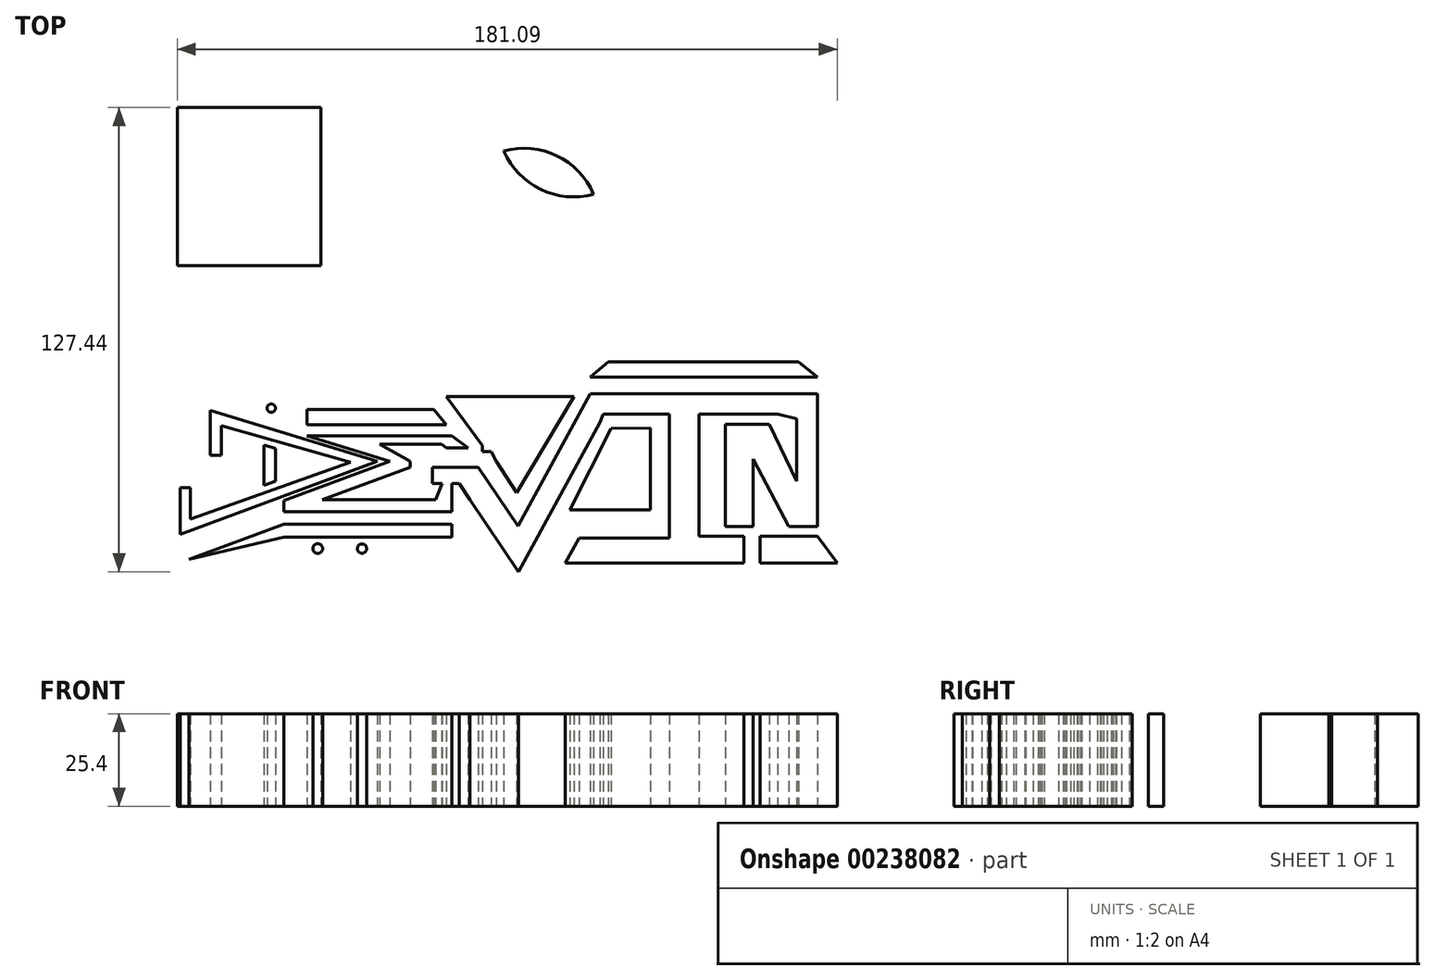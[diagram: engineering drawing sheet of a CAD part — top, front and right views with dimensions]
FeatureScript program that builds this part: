
annotation { "Feature Type Name" : "Feature", "Feature Type Description" : "" }
export const myFeature = defineFeature(function(context is Context, id is Id, definition is map)
    precondition{}
    {
        {
            var Q0;
            Q0=qCreatedBy(makeId("Top.planeOp"),FACE);
            var sketch = newSketch(context, id + "F0", { "sketchPlane" : qUnion([Q0])});
            skLineSegment(sketch, "E0.bottom", {"start": v(-55, 61.65) * mm, "end": v(-22, 61.65) * mm});
            skLineSegment(sketch, "E0.top", {"start": v(-61.34, 18.26) * mm, "end": v(-22, 18.26) * mm});
            skLineSegment(sketch, "E0.left", {"start": v(-61.34, 55.3) * mm, "end": v(-61.34, 18.26) * mm});
            skLineSegment(sketch, "E0.right", {"start": v(-22, 61.65) * mm, "end": v(-22, 18.26) * mm});
            skLineSegment(sketch, "E1.bottom", {"start": v(-41.67, 61.65) * mm, "end": v(-28.35, 61.65) * mm});
            skLineSegment(sketch, "E1.top", {"start": v(-41.67, 39.95) * mm, "end": v(-22, 39.95) * mm});
            skLineSegment(sketch, "E1.left", {"start": v(-41.67, 61.65) * mm, "end": v(-41.67, 39.95) * mm});
            skLineSegment(sketch, "E1.right", {"start": v(-22, 55.3) * mm, "end": v(-22, 39.95) * mm});
            skLineSegment(sketch, "E2.bottom", {"start": v(-41.67, 18.26) * mm, "end": v(-28.35, 18.26) * mm});
            skLineSegment(sketch, "E2.left", {"start": v(-41.67, 18.26) * mm, "end": v(-41.67, 39.95) * mm});
            skLineSegment(sketch, "E2.right", {"start": v(-22, 24.61) * mm, "end": v(-22, 39.95) * mm});
            skLineSegment(sketch, "E3.bottom", {"start": v(-41.67, 39.95) * mm, "end": v(-61.34, 39.95) * mm});
            skLineSegment(sketch, "E3.top", {"start": v(-41.67, 61.65) * mm, "end": v(-61.34, 61.65) * mm});
            skLineSegment(sketch, "E3.left", {"start": v(-41.67, 39.95) * mm, "end": v(-41.67, 61.65) * mm});
            skLineSegment(sketch, "E3.right", {"start": v(-61.34, 39.95) * mm, "end": v(-61.34, 61.65) * mm});
            skLineSegment(sketch, "E4.bottom", {"start": v(-55, 18.26) * mm, "end": v(-41.67, 18.26) * mm});
            skLineSegment(sketch, "E4.top", {"start": v(-61.34, 39.95) * mm, "end": v(-41.67, 39.95) * mm});
            skLineSegment(sketch, "E4.left", {"start": v(-61.34, 24.61) * mm, "end": v(-61.34, 39.95) * mm});
            skPoint(sketch, "E5.visualSharp", {"position": v(-61.34, 61.65) * mm});
            skArc(sketch, "E5.filletArc", {"start": v(-55, 61.65) * mm, "mid": v(-59.48, 59.79) * mm, "end": v(-61.34, 55.3) * mm});
            skPoint(sketch, "E6.visualSharp", {"position": v(-22, 61.65) * mm});
            skArc(sketch, "E6.filletArc", {"start": v(-22, 55.3) * mm, "mid": v(-23.86, 59.79) * mm, "end": v(-28.35, 61.65) * mm});
            skPoint(sketch, "E7.visualSharp", {"position": v(-22, 18.26) * mm});
            skArc(sketch, "E7.filletArc", {"start": v(-28.35, 18.26) * mm, "mid": v(-23.86, 20.12) * mm, "end": v(-22, 24.61) * mm});
            skPoint(sketch, "E8.visualSharp", {"position": v(-61.34, 18.26) * mm});
            skArc(sketch, "E8.filletArc", {"start": v(-61.34, 24.61) * mm, "mid": v(-59.48, 20.12) * mm, "end": v(-55, 18.26) * mm});
            skArc(sketch, "E9", {"start": v(13.52, 35.01) * mm, "mid": v(48.5, 14.76) * mm, "end": v(28.25, 49.74) * mm});
            skArc(sketch, "E10", {"start": v(28.25, 49.74) * mm, "mid": v(67.3, 51.66) * mm, "end": v(36.52, 75.77) * mm});
            skLineSegment(sketch, "E11", {"start": v(-52.26, -21.5) * mm, "end": v(-6.46, -35.41) * mm});
            skLineSegment(sketch, "E12", {"start": v(-6.46, -35.41) * mm, "end": v(-60.54, -55.6) * mm});
            skLineSegment(sketch, "E13", {"start": v(-60.54, -55.6) * mm, "end": v(-60.54, -42.68) * mm});
            skLineSegment(sketch, "E14", {"start": v(-52.26, -21.5) * mm, "end": v(-52.26, -33.8) * mm});
            skLineSegment(sketch, "E15", {"start": v(-52.26, -33.8) * mm, "end": v(-49.26, -33.8) * mm});
            skLineSegment(sketch, "E16", {"start": v(-49.26, -33.8) * mm, "end": v(-49.26, -25.67) * mm});
            skLineSegment(sketch, "E17", {"start": v(-49.26, -25.67) * mm, "end": v(-13.79, -35.76) * mm});
            skLineSegment(sketch, "E18", {"start": v(-13.79, -35.76) * mm, "end": v(-57.75, -51.38) * mm});
            skLineSegment(sketch, "E19", {"start": v(-57.75, -51.38) * mm, "end": v(-57.75, -42.68) * mm});
            skLineSegment(sketch, "E20", {"start": v(-57.75, -42.68) * mm, "end": v(-60.54, -42.68) * mm});
            skLineSegment(sketch, "E21", {"start": v(-37.52, -31.02) * mm, "end": v(-34.41, -31.9) * mm});
            skLineSegment(sketch, "E22", {"start": v(-34.41, -31.9) * mm, "end": v(-34.41, -40.97) * mm});
            skLineSegment(sketch, "E23", {"start": v(-34.41, -40.97) * mm, "end": v(-37.52, -42.07) * mm});
            skLineSegment(sketch, "E24", {"start": v(-37.52, -42.07) * mm, "end": v(-37.52, -31.02) * mm});
            skLineSegment(sketch, "E25", {"start": v(-3, -35.41) * mm, "end": v(-25.8, -28.49) * mm});
            skLineSegment(sketch, "E26", {"start": v(-25.8, -28.49) * mm, "end": v(14.04, -28.49) * mm});
            skLineSegment(sketch, "E27", {"start": v(-3, -35.41) * mm, "end": v(-32.08, -46.26) * mm});
            skLineSegment(sketch, "E28", {"start": v(-32.08, -46.26) * mm, "end": v(-32.08, -49.36) * mm});
            skLineSegment(sketch, "E29", {"start": v(-32.08, -49.36) * mm, "end": v(14.04, -49.36) * mm});
            skLineSegment(sketch, "E30", {"start": v(14.04, -28.49) * mm, "end": v(18.42, -31.74) * mm});
            skLineSegment(sketch, "E31", {"start": v(18.42, -31.74) * mm, "end": v(12.52, -31.74) * mm});
            skLineSegment(sketch, "E32", {"start": v(12.52, -31.74) * mm, "end": v(11.16, -30.73) * mm});
            skLineSegment(sketch, "E33", {"start": v(11.16, -30.73) * mm, "end": v(-5.77, -30.73) * mm});
            skLineSegment(sketch, "E34", {"start": v(-5.77, -30.73) * mm, "end": v(2.61, -35.41) * mm});
            skLineSegment(sketch, "E35", {"start": v(2.61, -35.41) * mm, "end": v(2.61, -37.07) * mm});
            skLineSegment(sketch, "E36", {"start": v(2.61, -37.07) * mm, "end": v(-21.5, -46.07) * mm});
            skLineSegment(sketch, "E37", {"start": v(-21.5, -46.07) * mm, "end": v(9.56, -46.07) * mm});
            skPoint(sketch, "E38.endSnap0", {"position": v(-9.44, -41.57) * mm});
            skLineSegment(sketch, "E39", {"start": v(11.28, -41.57) * mm, "end": v(9.56, -46.07) * mm});
            skLineSegment(sketch, "E40", {"start": v(11.28, -41.57) * mm, "end": v(8.61, -41.57) * mm});
            skLineSegment(sketch, "E41", {"start": v(8.61, -41.57) * mm, "end": v(8.61, -37.07) * mm});
            skLineSegment(sketch, "E42", {"start": v(8.61, -37.07) * mm, "end": v(21.18, -37.07) * mm});
            skLineSegment(sketch, "E43", {"start": v(21.18, -37.07) * mm, "end": v(32.14, -53.26) * mm});
            skLineSegment(sketch, "E44", {"start": v(32.14, -53.26) * mm, "end": v(48.9, -22.5) * mm});
            skLineSegment(sketch, "E45", {"start": v(18.9, -46.07) * mm, "end": v(32.25, -65.8) * mm});
            skLineSegment(sketch, "E46", {"start": v(32.25, -65.8) * mm, "end": v(54.59, -24.78) * mm});
            skLineSegment(sketch, "E47", {"start": v(14.04, -49.36) * mm, "end": v(14.04, -41.57) * mm});
            skLineSegment(sketch, "E48", {"start": v(18.9, -46.07) * mm, "end": v(16.04, -41.57) * mm});
            skLineSegment(sketch, "E49", {"start": v(16.04, -41.57) * mm, "end": v(14.04, -41.57) * mm});
            skLineSegment(sketch, "E50", {"start": v(48.9, -22.5) * mm, "end": v(51.96, -16.88) * mm});
            skLineSegment(sketch, "E51", {"start": v(51.96, -16.88) * mm, "end": v(103.46, -16.88) * mm});
            skLineSegment(sketch, "E52", {"start": v(55.47, -22.5) * mm, "end": v(54.59, -24.78) * mm});
            skLineSegment(sketch, "E53", {"start": v(73.66, -22.5) * mm, "end": v(73.66, -56.6) * mm});
            skLineSegment(sketch, "E54", {"start": v(73.66, -56.6) * mm, "end": v(48.9, -56.6) * mm});
            skLineSegment(sketch, "E55", {"start": v(48.9, -56.6) * mm, "end": v(45.17, -63.43) * mm});
            skLineSegment(sketch, "E56", {"start": v(45.17, -63.43) * mm, "end": v(94.13, -63.43) * mm});
            skLineSegment(sketch, "E57", {"start": v(94.13, -63.43) * mm, "end": v(94.13, -56.03) * mm});
            skLineSegment(sketch, "E58", {"start": v(94.13, -56.03) * mm, "end": v(81.75, -56.03) * mm});
            skLineSegment(sketch, "E59", {"start": v(81.75, -56.03) * mm, "end": v(81.75, -22.5) * mm});
            skLineSegment(sketch, "E60", {"start": v(55.47, -22.5) * mm, "end": v(73.66, -22.5) * mm});
            skLineSegment(sketch, "E61", {"start": v(81.75, -22.5) * mm, "end": v(103.46, -22.5) * mm});
            skLineSegment(sketch, "E62", {"start": v(89.07, -29.3) * mm, "end": v(89.07, -53.32) * mm});
            skLineSegment(sketch, "E63", {"start": v(89.07, -53.32) * mm, "end": v(96.66, -53.32) * mm});
            skLineSegment(sketch, "E64", {"start": v(96.66, -53.32) * mm, "end": v(96.66, -34.86) * mm});
            skLineSegment(sketch, "E65", {"start": v(96.66, -34.86) * mm, "end": v(106.4, -53.32) * mm});
            skLineSegment(sketch, "E66", {"start": v(106.4, -53.32) * mm, "end": v(114.33, -53.32) * mm});
            skLineSegment(sketch, "E67", {"start": v(114.33, -53.32) * mm, "end": v(114.33, -16.88) * mm});
            skLineSegment(sketch, "E68", {"start": v(114.33, -16.88) * mm, "end": v(103.46, -16.88) * mm});
            skLineSegment(sketch, "E69", {"start": v(89.07, -29.3) * mm, "end": v(89.07, -25.34) * mm});
            skLineSegment(sketch, "E70", {"start": v(89.07, -25.34) * mm, "end": v(101.08, -25.34) * mm});
            skLineSegment(sketch, "E71", {"start": v(101.08, -25.34) * mm, "end": v(108.55, -40.97) * mm});
            skLineSegment(sketch, "E72", {"start": v(108.55, -40.97) * mm, "end": v(108.55, -23.76) * mm});
            skLineSegment(sketch, "E73", {"start": v(108.55, -23.76) * mm, "end": v(103.46, -22.5) * mm});
            skLineSegment(sketch, "E74", {"start": v(57.66, -26.43) * mm, "end": v(46.43, -48.77) * mm});
            skLineSegment(sketch, "E75", {"start": v(46.43, -48.77) * mm, "end": v(68.45, -48.77) * mm});
            skLineSegment(sketch, "E76", {"start": v(68.45, -48.77) * mm, "end": v(68.45, -26.32) * mm});
            skLineSegment(sketch, "E77", {"start": v(68.45, -26.32) * mm, "end": v(57.66, -26.43) * mm});
            skLineSegment(sketch, "E78", {"start": v(26.23, -35.41) * mm, "end": v(31.79, -44.07) * mm});
            skLineSegment(sketch, "E79", {"start": v(31.79, -44.07) * mm, "end": v(47.5, -17.67) * mm});
            skLineSegment(sketch, "E80", {"start": v(47.5, -17.67) * mm, "end": v(12.44, -17.67) * mm});
            skLineSegment(sketch, "E81", {"start": v(12.44, -17.67) * mm, "end": v(22.38, -31.13) * mm});
            skLineSegment(sketch, "E82", {"start": v(22.38, -31.13) * mm, "end": v(22.38, -32.84) * mm});
            skLineSegment(sketch, "E83", {"start": v(22.38, -32.84) * mm, "end": v(24.73, -32.84) * mm});
            skLineSegment(sketch, "E84", {"start": v(24.73, -32.84) * mm, "end": v(26.23, -35.41) * mm});
            skCircle(sketch, "E85", {"center": v(-35.56, -20.87) * mm, "radius": 1.15 * mm});
            skLineSegment(sketch, "E86", {"start": v(14.04, -52.68) * mm, "end": v(-32.08, -52.68) * mm});
            skLineSegment(sketch, "E87", {"start": v(-32.08, -52.68) * mm, "end": v(-32.08, -56.32) * mm});
            skLineSegment(sketch, "E88", {"start": v(-32.08, -56.32) * mm, "end": v(14.04, -56.32) * mm});
            skLineSegment(sketch, "E89", {"start": v(14.04, -56.32) * mm, "end": v(14.04, -52.68) * mm});
            skLineSegment(sketch, "E90", {"start": v(-32.08, -52.68) * mm, "end": v(-58.13, -62.4) * mm});
            skLineSegment(sketch, "E91", {"start": v(-58.13, -62.4) * mm, "end": v(-32.08, -56.32) * mm});
            skCircle(sketch, "E92", {"center": v(-22.8, -59.43) * mm, "radius": 1.34 * mm});
            skCircle(sketch, "E93", {"center": v(-10.66, -59.43) * mm, "radius": 1.28 * mm});
            skLineSegment(sketch, "E94", {"start": v(51.96, -12.41) * mm, "end": v(114.33, -12.41) * mm});
            skLineSegment(sketch, "E95", {"start": v(114.33, -12.41) * mm, "end": v(109.16, -8.17) * mm});
            skLineSegment(sketch, "E96", {"start": v(109.16, -8.17) * mm, "end": v(56.9, -8.17) * mm});
            skLineSegment(sketch, "E97", {"start": v(56.9, -8.17) * mm, "end": v(51.96, -12.41) * mm});
            skLineSegment(sketch, "E98", {"start": v(98.63, -63.43) * mm, "end": v(98.63, -56.03) * mm});
            skLineSegment(sketch, "E99", {"start": v(98.63, -56.03) * mm, "end": v(114.33, -56.03) * mm});
            skLineSegment(sketch, "E100", {"start": v(114.33, -56.03) * mm, "end": v(119.75, -63.43) * mm});
            skLineSegment(sketch, "E101", {"start": v(119.75, -63.43) * mm, "end": v(98.63, -63.43) * mm});
            skLineSegment(sketch, "E102", {"start": v(-25.8, -25.38) * mm, "end": v(12.43, -25.38) * mm});
            skLineSegment(sketch, "E103", {"start": v(12.43, -25.38) * mm, "end": v(9, -21.19) * mm});
            skLineSegment(sketch, "E104", {"start": v(9, -21.19) * mm, "end": v(-25.8, -21.19) * mm});
            skLineSegment(sketch, "E105", {"start": v(-25.8, -21.19) * mm, "end": v(-25.8, -25.38) * mm});
            skSolve(sketch);
        }
        {
            var Q0;
            Q0=makeQuery(id+"F0.imprint","IMPRINT",FACE,{"disambiguationData":[TD([[makeQuery(id+"F0.imprint","IMPRINT",EDGE,{"derivedFrom":sQuery(id+"F0.wireOp",EDGE,"E11")}),-1.0]])]});
            var Q1;
            Q1=makeQuery(id+"F0.imprint","IMPRINT",FACE,{"disambiguationData":[TD([[makeQuery(id+"F0.imprint","IMPRINT",EDGE,{"derivedFrom":sQuery(id+"F0.wireOp",EDGE,"E21")}),-1.0]])]});
            var Q2;
            Q2=makeQuery(id+"F0.imprint","IMPRINT",FACE,{"disambiguationData":[TD([[makeQuery(id+"F0.imprint","IMPRINT",EDGE,{"derivedFrom":sQuery(id+"F0.wireOp",EDGE,"E25")}),-1.0]])]});
            var Q3;
            Q3=makeQuery(id+"F0.imprint","IMPRINT",FACE,{"disambiguationData":[TD([[makeQuery(id+"F0.imprint","IMPRINT",EDGE,{"derivedFrom":sQuery(id+"F0.wireOp",EDGE,"E74")}),1.0]])]});
            var Q4;
            Q4=makeQuery(id+"F0.imprint","IMPRINT",FACE,{"disambiguationData":[TD([[makeQuery(id+"F0.imprint","IMPRINT",EDGE,{"derivedFrom":sQuery(id+"F0.wireOp",EDGE,"E78")}),1.0]])]});
            var Q5;
            Q5=makeQuery(id+"F0.imprint","IMPRINT",FACE,{"disambiguationData":[TD([[makeQuery(id+"F0.imprint","IMPRINT",EDGE,{"derivedFrom":sQuery(id+"F0.wireOp",EDGE,"vDCnIXTR-u0rO-dLhL-Y9qB-n0xIWBPPiKpz")}),1.0]])]});
            var Q6;
            Q6=makeQuery(id+"F0.imprint","IMPRINT",FACE,{"disambiguationData":[TD([[makeQuery(id+"F0.imprint","IMPRINT",EDGE,{"derivedFrom":sQuery(id+"F0.wireOp",EDGE,"E85")}),1.0]])]});
            extrude(context, id + "F1", {"entities" : qUnion([Q0, Q1, Q2, Q3, Q4, Q5, Q6]), "depth" : 25.4 * mm});
        }
        {
            var Q0;
            Q0=makeQuery(id+"F0.imprint","IMPRINT",FACE,{"disambiguationData":[TD([[makeQuery(id+"F0.imprint","IMPRINT",EDGE,{"derivedFrom":sQuery(id+"F0.wireOp",EDGE,"E86")}),1.0]])]});
            var Q1;
            Q1=makeQuery(id+"F0.imprint","IMPRINT",FACE,{"disambiguationData":[TD([[makeQuery(id+"F0.imprint","IMPRINT",EDGE,{"derivedFrom":sQuery(id+"F0.wireOp",EDGE,"E87")}),-1.0]])]});
            var Q2;
            Q2=makeQuery(id+"F0.imprint","IMPRINT",FACE,{"disambiguationData":[TD([[makeQuery(id+"F0.imprint","IMPRINT",EDGE,{"derivedFrom":sQuery(id+"F0.wireOp",EDGE,"E92")}),1.0]])]});
            var Q3;
            Q3=makeQuery(id+"F0.imprint","IMPRINT",FACE,{"disambiguationData":[TD([[makeQuery(id+"F0.imprint","IMPRINT",EDGE,{"derivedFrom":sQuery(id+"F0.wireOp",EDGE,"E93")}),1.0]])]});
            extrude(context, id + "F2", {"entities" : qUnion([Q0, Q1, Q2, Q3]), "depth" : 25.4 * mm});
        }
        {
            var Q0;
            Q0=makeQuery(id+"F0.imprint","IMPRINT",FACE,{"disambiguationData":[TD([[makeQuery(id+"F0.imprint","IMPRINT",EDGE,{"derivedFrom":sQuery(id+"F0.wireOp",EDGE,"E94")}),1.0]])]});
            extrude(context, id + "F3", {"entities" : qUnion([Q0]), "depth" : 25.4 * mm});
        }
        {
            var Q0;
            Q0 = qSketchRegion(id + "F0", true);
            extrude(context, id + "F4", {"entities" : qUnion([Q0]), "depth" : 25.4 * mm});
        }
        {
            var Q0;
            Q0 = qSketchRegion(id + "F0", true);
            extrude(context, id + "F5", {"entities" : qUnion([Q0]), "depth" : 25.4 * mm});
        }
    });
